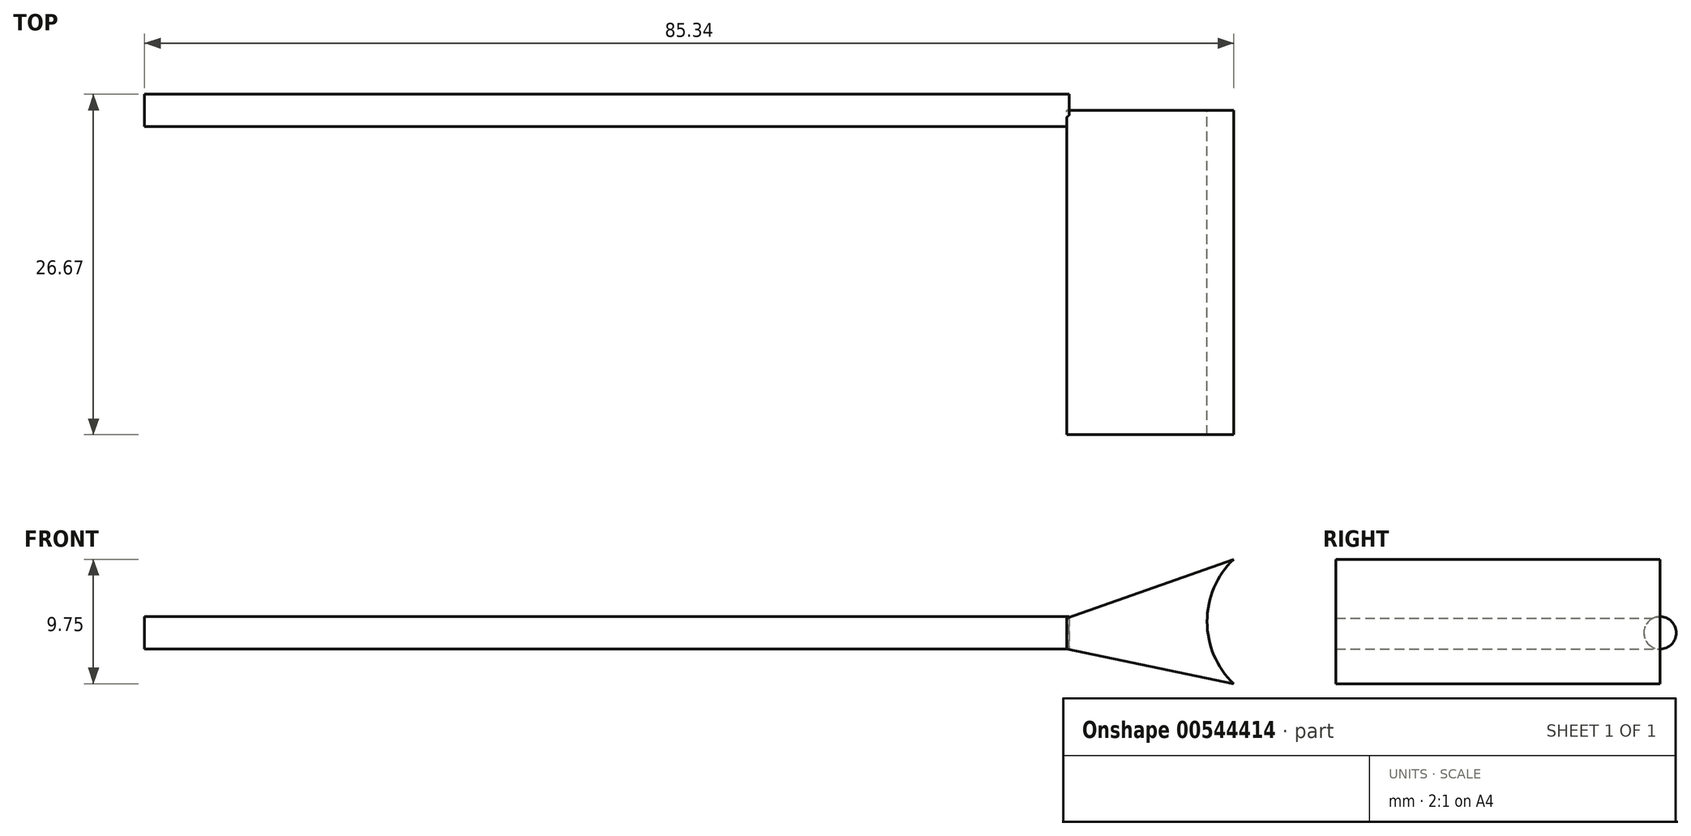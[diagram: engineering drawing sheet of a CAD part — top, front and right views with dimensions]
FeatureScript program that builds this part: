
annotation { "Feature Type Name" : "Feature", "Feature Type Description" : "" }
export const myFeature = defineFeature(function(context is Context, id is Id, definition is map)
    precondition{}
    {
        {
            var Q0;
            Q0=qCreatedBy(makeId("Top.planeOp"),FACE);
            var sketch = newSketch(context, id + "F0", { "sketchPlane" : qUnion([Q0])});
            skLineSegment(sketch, "E0", {"start": v(0, 0) * mm, "end": v(72.45, 0) * mm});
            skLineSegment(sketch, "E1.0", {"start": v(0, -1.27) * mm, "end": v(72.45, -1.27) * mm});
            skLineSegment(sketch, "E2", {"start": v(72.45, 0) * mm, "end": v(72.45, -1.27) * mm});
            skLineSegment(sketch, "E3", {"start": v(0, 0) * mm, "end": v(0, -1.27) * mm});
            skSolve(sketch);
        }
        {
            var Q0;
            Q0=makeQuery(id+"F0.imprint","IMPRINT",FACE,{"disambiguationData":[TD([[makeQuery(id+"F0.imprint","IMPRINT",EDGE,{"derivedFrom":sQuery(id+"F0.wireOp",EDGE,"E0")}),-1.0]])]});
            var Q1;
            Q1=sQuery(id+"F0.wireOp",EDGE,"E0");
            revolve(context, id + "F1", {"entities" : qUnion([Q0]), "axis" : qUnion([Q1]), "revolveType" : RevolveType.FULL});
        }
        {
            var Q0;
            Q0=qCreatedBy(makeId("Front.planeOp"),FACE);
            var sketch = newSketch(context, id + "F2", { "sketchPlane" : qUnion([Q0])});
            skLineSegment(sketch, "E4", {"start": v(85.34, 5.77) * mm, "end": v(72.24, 1.15) * mm});
            skLineSegment(sketch, "E5", {"start": v(72.24, 1.15) * mm, "end": v(72.24, -1.27) * mm});
            skLineSegment(sketch, "E6", {"start": v(72.24, -1.27) * mm, "end": v(85.34, -3.98) * mm});
            skPoint(sketch, "E7.end.orphan", {"position": v(85.34, 0) * mm});
            skArc(sketch, "E8", {"start": v(85.34, 5.77) * mm, "mid": v(83.25, 0.9) * mm, "end": v(85.34, -3.98) * mm});
            skSolve(sketch);
        }
        {
            var Q0;
            Q0=makeQuery(id+"F2.imprint","IMPRINT",FACE,{"disambiguationData":[TD([[makeQuery(id+"F2.imprint","IMPRINT",EDGE,{"derivedFrom":sQuery(id+"F2.wireOp",EDGE,"E4")}),1.0]])]});
            extrude(context, id + "F3", {"entities" : qUnion([Q0]), "operationType" : NewBodyOperationType.ADD, "depth" : 25.4 * mm, "offsetDistance" : 25.4 * mm});
        }
    });
